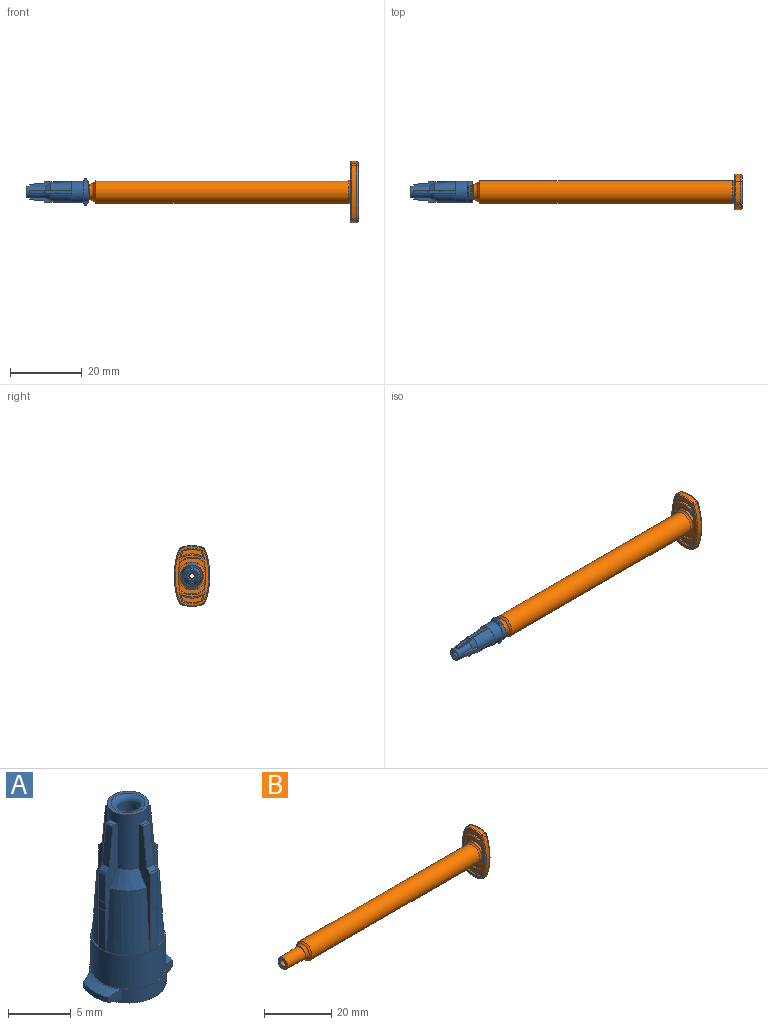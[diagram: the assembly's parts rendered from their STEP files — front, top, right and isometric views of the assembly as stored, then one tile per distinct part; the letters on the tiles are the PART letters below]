
ASSEMBLY  parts=2 mates=1
PART A: 78 faces, bbox 7.9x6.2x17.4 mm
  f0: plane 5.9x5.9mm, normal (0,0,1), area 1.6mm2, adj f1,f3,f5,f14,f15,f44,f46,f47
  f1: cone r=2.5mm half-angle=3.3deg, axis (0,0,-1), area 20.4mm2, adj f0,f2,f47,f77
  f2: cone r=1.65mm half-angle=29.5deg, axis (0,0,-1), area 4.2mm2, adj f1,f17,f47,f77
  f3: cone r=2.5mm half-angle=3.3deg, axis (0,0,-1), area 20.4mm2, adj f0,f4,f46,f67
  f4: cone r=1.65mm half-angle=29.5deg, axis (0,0,-1), area 4.2mm2, adj f3,f17,f46,f67
  f5: cone r=2.5mm half-angle=3.3deg, axis (0,0,-1), area 20.4mm2, adj f0,f6,f57,f76
  f6: cone r=1.65mm half-angle=29.5deg, axis (0,0,-1), area 4.2mm2, adj f5,f17,f57,f76
  f7: cylinder r=3.89mm len=2.81mm, axis (0,0,1), area 1.4mm2, adj f10,f12,f35,f37
  f8: cylinder r=3.89mm len=2.81mm, axis (0,0,1), area 1.4mm2, adj f9,f11,f34,f36
  f9: cone r=3.05mm half-angle=75deg, axis (0,0,1), area 2.9mm2, adj f8,f33,f34,f36
  f10: cone r=3.05mm half-angle=75deg, axis (0,0,1), area 2.9mm2, adj f7,f33,f35,f37
  f11: cone r=3.89mm half-angle=65deg, axis (0,0,-1), area 3.1mm2, adj f8,f13,f34,f36
  f12: cone r=3.89mm half-angle=65deg, axis (0,0,-1), area 3.1mm2, adj f7,f13,f35,f37
  f13: cone r=2.95mm half-angle=89.9deg, axis (0,0,-1), area 1.9mm2, adj f11,f12,f14,f33
  f14: cylinder r=2.95mm len=5.9mm, axis (0,0,1), area 59.3mm2, adj f0,f13
  f15: cone r=2.5mm half-angle=3.3deg, axis (0,0,-1), area 20.4mm2, adj f0,f16,f56,f66
  f16: cone r=1.65mm half-angle=29.5deg, axis (0,0,-1), area 4.2mm2, adj f15,f17,f56,f66
  f17: cylinder r=1.65mm len=5.3mm, axis (0,0,1), area 41mm2, adj f2,f4,f6,f16,f18,f43,f46,f47
  f18: plane 3.3x3.3mm, normal (0,0,1), area 2.8mm2, adj f17,f19
  f19: torus R=1.35mm, axis (0,0,1), area 5.1mm2, adj f18,f20
  f20: cylinder r=0.85mm len=5.8mm, axis (0,0,1), area 31mm2, adj f19,f21
  f21: plane 1.7x1.7mm, normal (0,0,1), area 0.6mm2, adj f20,f22
  f22: cylinder r=0.72mm len=1.45mm, axis (0,0,1), area 3.6mm2, adj f21,f23
  f23: plane 2.7x2.7mm, normal (0,0,-1), area 4.1mm2, adj f22,f24
  f24: cylinder r=1.35mm len=2.7mm, axis (0,0,1), area 2.5mm2, adj f23,f25
  f25: torus R=1.37mm, axis (0,0,1), area 8.2mm2, adj f24,f26
  f26: cone r=1.89mm half-angle=1.7deg, axis (0,0,-1), area 7.4mm2, adj f25,f27
  f27: torus R=1.59mm, axis (0,0,1), area 2.6mm2, adj f26,f28
  f28: torus R=2.29mm, axis (0,0,1), area 10.2mm2, adj f27,f29
  f29: torus R=1.63mm, axis (0,0,1), area 2.7mm2, adj f28,f30
  f30: cone r=1.93mm half-angle=1.7deg, axis (0,0,-1), area 101.5mm2, adj f29,f31
  f31: torus R=2.41mm, axis (0,0,1), area 5.5mm2, adj f30,f32
  f32: plane 6.1x6.1mm, normal (0,0,-1), area 10.9mm2, adj f31,f33
  f33: cylinder r=3.05mm len=6.1mm, axis (0,0,1), area 16.7mm2, adj f9,f10,f13,f32,f34,f35,f36,f37
  f34: plane 1.25x1.22mm, normal (-0.29,0.96,0), area 0.9mm2, adj f8,f9,f11,f33
  f35: plane 1.25x1.22mm, normal (0.29,0.96,0), area 0.9mm2, adj f7,f10,f12,f33
  f36: plane 1.25x1.22mm, normal (-0.29,-0.96,0), area 0.9mm2, adj f8,f9,f11,f33
  f37: plane 1.25x1.22mm, normal (0.29,-0.96,0), area 0.9mm2, adj f7,f10,f12,f33
  f38: plane 2.7x0.8mm, normal (0,1,-0.01), area 2.2mm2, adj f39,f45,f46,f47
  f39: cylinder r=0.3mm len=0.8mm, axis (-1,0,0), area 0.2mm2, adj f38,f40,f46,f47
  f40: plane 0.8x0.32mm, normal (0,0.71,0.71), area 0.4mm2, adj f39,f41,f46,f47
  f41: plane 3.76x0.8mm, normal (0,0.99,0.1), area 3mm2, adj f40,f42,f46,f47
  f42: cylinder r=0.15mm len=0.8mm, axis (-1,0,0), area 0.2mm2, adj f41,f43,f46,f47
  f43: plane 0.8x0.36mm, normal (0,0,1), area 0.3mm2, adj f17,f42,f46,f47
  f44: plane 3.9x0.8mm, normal (0,1,0.01), area 3.1mm2, adj f0,f45,f46,f47
  f45: plane 0.8x0.77mm, normal (0,1,0), area 0.6mm2, adj f38,f44,f46,f47
  f46: plane 11.84x1.35mm, normal (1,0,0), area 5.9mm2, adj f0,f3,f4,f17,f38,f39,f40,f41
  f47: plane 11.84x1.35mm, normal (-1,0,0), area 5.9mm2, adj f0,f1,f2,f17,f38,f39,f40,f41
  f48: plane 0.8x0.36mm, normal (0,0,1), area 0.3mm2, adj f17,f49,f56,f57
  f49: cylinder r=0.15mm len=0.8mm, axis (-1,0,0), area 0.2mm2, adj f48,f50,f56,f57
  f50: plane 3.76x0.8mm, normal (0,-0.99,0.1), area 3mm2, adj f49,f51,f56,f57
  f51: plane 0.8x0.32mm, normal (0,-0.71,0.71), area 0.4mm2, adj f50,f52,f56,f57
  f52: cylinder r=0.3mm len=0.8mm, axis (-1,0,0), area 0.2mm2, adj f51,f53,f56,f57
  f53: plane 2.7x0.8mm, normal (0,-1,-0.01), area 2.2mm2, adj f52,f54,f56,f57
  f54: plane 0.8x0.77mm, normal (0,-1,0), area 0.6mm2, adj f53,f55,f56,f57
  f55: plane 3.9x0.8mm, normal (0,-1,0.01), area 3.1mm2, adj f0,f54,f56,f57
  f56: plane 11.84x1.35mm, normal (1,0,0), area 5.9mm2, adj f0,f15,f16,f17,f48,f49,f50,f51
  f57: plane 11.84x1.35mm, normal (-1,0,0), area 5.9mm2, adj f0,f5,f6,f17,f48,f49,f50,f51
  f58: plane 2.7x0.8mm, normal (1,0,-0.01), area 2.2mm2, adj f59,f65,f66,f67
  f59: cylinder r=0.3mm len=0.8mm, axis (0,1,0), area 0.2mm2, adj f58,f60,f66,f67
  f60: plane 0.8x0.32mm, normal (0.71,0,0.71), area 0.4mm2, adj f59,f61,f66,f67
  f61: plane 3.76x0.8mm, normal (0.99,0,0.1), area 3mm2, adj f60,f62,f66,f67
  f62: cylinder r=0.15mm len=0.8mm, axis (0,1,0), area 0.2mm2, adj f61,f63,f66,f67
  f63: plane 0.8x0.36mm, normal (0,0,1), area 0.3mm2, adj f17,f62,f66,f67
  f64: plane 3.9x0.8mm, normal (1,0,0.01), area 3.1mm2, adj f0,f65,f66,f67
  f65: plane 0.8x0.77mm, normal (1,0,0), area 0.6mm2, adj f58,f64,f66,f67
  f66: plane 11.84x1.35mm, normal (0,-1,0), area 5.9mm2, adj f0,f15,f16,f17,f58,f59,f60,f61
  f67: plane 11.84x1.35mm, normal (0,1,0), area 5.9mm2, adj f0,f3,f4,f17,f58,f59,f60,f61
  f68: plane 0.8x0.36mm, normal (0,0,1), area 0.3mm2, adj f17,f69,f76,f77
  f69: cylinder r=0.15mm len=0.8mm, axis (0,1,0), area 0.2mm2, adj f68,f70,f76,f77
  f70: plane 3.76x0.8mm, normal (-0.99,0,0.1), area 3mm2, adj f69,f71,f76,f77
  f71: plane 0.8x0.32mm, normal (-0.71,0,0.71), area 0.4mm2, adj f70,f72,f76,f77
  f72: cylinder r=0.3mm len=0.8mm, axis (0,1,0), area 0.2mm2, adj f71,f73,f76,f77
  f73: plane 2.7x0.8mm, normal (-1,0,-0.01), area 2.2mm2, adj f72,f74,f76,f77
  f74: plane 0.8x0.77mm, normal (-1,0,0), area 0.6mm2, adj f73,f75,f76,f77
  f75: plane 3.9x0.8mm, normal (-1,0,0.01), area 3.1mm2, adj f0,f74,f76,f77
  f76: plane 11.84x1.35mm, normal (0,-1,0), area 5.9mm2, adj f0,f5,f6,f17,f68,f69,f70,f71
  f77: plane 11.84x1.35mm, normal (0,1,0), area 5.9mm2, adj f0,f1,f2,f17,f68,f69,f70,f71
PART B: 74 faces, bbox 82.3x11x17.4 mm
  f0: plane 16.41x9.41mm, normal (-1,0,0), area 38.2mm2, adj f3,f34,f36,f39,f41,f48,f49,f50
  f1: cylinder r=8.5mm len=6.03mm, axis (1,0,0), area 8.6mm2, adj f25,f27,f49,f58
  f2: cylinder r=8.5mm len=6.03mm, axis (1,0,0), area 8.6mm2, adj f24,f26,f54,f61
  f3: torus R=3.8mm, axis (1,0,0), area 20.2mm2, adj f0,f4,f35,f38
  f4: cylinder r=3.2mm len=70.4mm, axis (1,0,0), area 1415.5mm2, adj f3,f5
  f5: cone r=3.2mm half-angle=46.7deg, axis (1,0,0), area 13.7mm2, adj f4,f6
  f6: torus R=3.69mm, axis (1,0,0), area 18mm2, adj f5,f7
  f7: cone r=2.19mm half-angle=0deg, axis (1,0,0), area 1.4mm2, adj f6,f8
  f8: cone r=1.97mm half-angle=1.7deg, axis (1,0,0), area 94.8mm2, adj f7,f9
  f9: torus R=1.72mm, axis (1,0,0), area 4.5mm2, adj f8,f10
  f10: plane 3.44x3.44mm, normal (-1,0,0), area 3.5mm2, adj f9,f11
  f11: cone r=1.35mm half-angle=15deg, axis (-1,0,0), area 1.7mm2, adj f10,f12
  f12: plane 2.6x2.6mm, normal (-1,0,0), area 1.8mm2, adj f11,f13
  f13: cone r=1.29mm half-angle=1.6deg, axis (1,0,0), area 62mm2, adj f12,f14
  f14: torus R=2.29mm, axis (1,0,0), area 6.9mm2, adj f13,f15
  f15: cone r=1.6mm half-angle=46.7deg, axis (1,0,0), area 12.9mm2, adj f14,f16
  f16: cylinder r=2.35mm len=67.56mm, axis (1,0,0), area 999.6mm2, adj f15,f17
  f17: cone r=2.36mm half-angle=0.8deg, axis (1,0,0), area 5.2mm2, adj f16,f18
  f18: cylinder r=2.36mm len=4.72mm, axis (1,0,0), area 19.3mm2, adj f17,f19
  f19: cone r=2.36mm half-angle=18.9deg, axis (-1,0,0), area 5.3mm2, adj f18,f20
  f20: cone r=2.93mm half-angle=14.8deg, axis (1,0,0), area 43.6mm2, adj f19,f21
  f21: plane 16.41x9.41mm, normal (1,0,0), area 105.7mm2, adj f20,f56,f57,f58,f59,f60,f61,f62
  f22: cylinder r=20mm len=14.76mm, axis (1,0,0), area 21.2mm2, adj f24,f25,f53,f62
  f23: cylinder r=20mm len=14.76mm, axis (1,0,0), area 21.2mm2, adj f26,f27,f50,f57
  f24: bspline ~2.2x0.58mm, area 1.2mm2, adj f2,f22,f55,f63
  f25: bspline ~2.2x0.58mm, area 1.2mm2, adj f1,f22,f51,f60
  f26: bspline ~2.2x0.58mm, area 1.2mm2, adj f2,f23,f52,f59
  f27: bspline ~2.2x0.58mm, area 1.2mm2, adj f1,f23,f48,f56
  f28: cylinder r=6.14mm len=6.12mm, axis (-1,0,0), area 1.9mm2, adj f29,f31,f32,f67
  f29: cylinder r=20mm len=1.56mm, axis (-1,0,0), area 0.5mm2, adj f28,f30,f32,f66
  f30: cylinder r=7.34mm len=5.12mm, axis (-1,0,0), area 1.6mm2, adj f29,f31,f32,f68
  f31: cylinder r=20mm len=1.56mm, axis (-1,0,0), area 0.5mm2, adj f28,f30,f32,f69
  f32: plane 6.12x2.02mm, normal (-1,0,0), area 7mm2, adj f28,f29,f30,f31
  f33: cylinder r=4.98mm len=6.91mm, axis (-1,0,0), area 2.3mm2, adj f34,f36,f37,f65
  f34: cylinder r=20mm len=3.64mm, axis (-1,0,0), area 2mm2, adj f0,f33,f35,f37,f65
  f35: cylinder r=3.8mm len=7.55mm, axis (-1,0,0), area 6.6mm2, adj f3,f34,f36,f37
  f36: cylinder r=20mm len=3.64mm, axis (-1,0,0), area 2mm2, adj f0,f33,f35,f37,f65
  f37: plane 7.55x4.55mm, normal (-1,0,0), area 10.3mm2, adj f33,f34,f35,f36
  f38: cylinder r=3.8mm len=7.55mm, axis (-1,0,0), area 6.6mm2, adj f3,f39,f41,f42
  f39: cylinder r=20mm len=3.64mm, axis (-1,0,0), area 2mm2, adj f0,f38,f40,f42,f64
  f40: cylinder r=4.98mm len=6.91mm, axis (-1,0,0), area 2.3mm2, adj f39,f41,f42,f64
  f41: cylinder r=20mm len=3.64mm, axis (-1,0,0), area 2mm2, adj f0,f38,f40,f42,f64
  f42: plane 7.55x4.55mm, normal (-1,0,0), area 10.3mm2, adj f38,f39,f40,f41
  f43: cylinder r=7.34mm len=5.12mm, axis (-1,0,0), area 1.6mm2, adj f44,f46,f47,f71
  f44: cylinder r=20mm len=1.56mm, axis (-1,0,0), area 0.5mm2, adj f43,f45,f47,f70
  f45: cylinder r=6.14mm len=6.12mm, axis (-1,0,0), area 1.9mm2, adj f44,f46,f47,f72
  f46: cylinder r=20mm len=1.56mm, axis (-1,0,0), area 0.5mm2, adj f43,f45,f47,f73
  f47: plane 6.12x2.02mm, normal (-1,0,0), area 7mm2, adj f43,f44,f45,f46
  f48: bspline ~0.68x0.68mm, area 0.4mm2, adj f0,f27,f49,f50
  f49: bspline ~6.03x1.02mm, area 3mm2, adj f0,f1,f48,f51
  f50: bspline ~14.76x2.17mm, area 7.3mm2, adj f0,f23,f48,f52
  f51: bspline ~0.68x0.68mm, area 0.4mm2, adj f0,f25,f49,f53
  f52: bspline ~0.68x0.68mm, area 0.4mm2, adj f0,f26,f50,f54
  f53: bspline ~14.76x2.17mm, area 7.3mm2, adj f0,f22,f51,f55
  f54: bspline ~6.03x1.02mm, area 3mm2, adj f0,f2,f52,f55
  f55: bspline ~0.68x0.68mm, area 0.4mm2, adj f0,f24,f53,f54
  f56: bspline ~0.68x0.68mm, area 0.4mm2, adj f21,f27,f57,f58
  f57: bspline ~14.76x2.17mm, area 7.3mm2, adj f21,f23,f56,f59
  f58: bspline ~6.03x1.02mm, area 3mm2, adj f1,f21,f56,f60
  f59: bspline ~0.68x0.68mm, area 0.4mm2, adj f21,f26,f57,f61
  f60: bspline ~0.68x0.68mm, area 0.4mm2, adj f21,f25,f58,f62
  f61: bspline ~6.03x1.02mm, area 3mm2, adj f2,f21,f59,f63
  f62: bspline ~14.76x2.17mm, area 7.3mm2, adj f21,f22,f60,f63
  f63: bspline ~0.68x0.68mm, area 0.4mm2, adj f21,f24,f61,f62
  f64: bspline ~7.89x2.13mm, area 3.6mm2, adj f0,f39,f40,f41
  f65: bspline ~7.89x2.13mm, area 3.6mm2, adj f0,f33,f34,f36
  f66: bspline ~2.73x1.09mm, area 1mm2, adj f0,f29,f67,f68
  f67: bspline ~7.45x1.5mm, area 3.5mm2, adj f0,f28,f66,f69
  f68: bspline ~5.59x0.81mm, area 2.7mm2, adj f0,f30,f66,f69
  f69: bspline ~2.73x1.09mm, area 1mm2, adj f0,f31,f67,f68
  f70: bspline ~2.73x1.09mm, area 1mm2, adj f0,f44,f71,f72
  f71: bspline ~5.59x0.81mm, area 2.7mm2, adj f0,f43,f70,f73
  f72: bspline ~7.45x1.5mm, area 3.5mm2, adj f0,f45,f70,f73
  f73: bspline ~2.73x1.09mm, area 1mm2, adj f0,f46,f71,f72
PLACE A rot(axis=(0.71,0,-0.71),180deg) t=(-44.92,-0.28,9.02)mm
PLACE B t=(30.18,-0.28,9.02)mm
MATE slider A.f1 <-> B.f11  axis (1,0,0) through (-44.92,-0.28,9.02)mm
